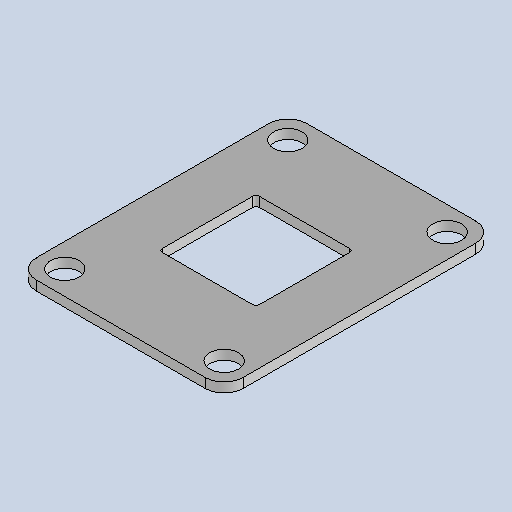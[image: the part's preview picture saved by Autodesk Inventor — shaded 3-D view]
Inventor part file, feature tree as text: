
AUTODESK INVENTOR PART (.ipt)
format: ipt  version: 2025.1 (Build 291241020, 241B)  size: 329,728 bytes
history: native  units: mm
features: other x3, chamfer x2, sketch x2, sheet_metal_op x1
ambient origin geometry x8: Origin, YZ Plane, XZ Plane, XY Plane, X Axis, Y Axis, Z Axis, Center Point
bodies: Body1 (feature_tree)
feature tree (8):
  sheet_metal_op  "Face3"
  chamfer  "Corner Round1"
  chamfer  "Corner Round2"
  sketch  "Sketch1"  dims[d154=65.0mm]
  other  "Plate5"
  sketch  "Sketch9"  dims[d155=85.0mm d156=3.0mm d172=30.5mm d173=70.0mm d174=9.0mm d175=50.0mm d176=3.0mm d177=0.0mm d178=6.0mm d179=1.0mm]
  other  "Cut2"
  other  "Definition1"
